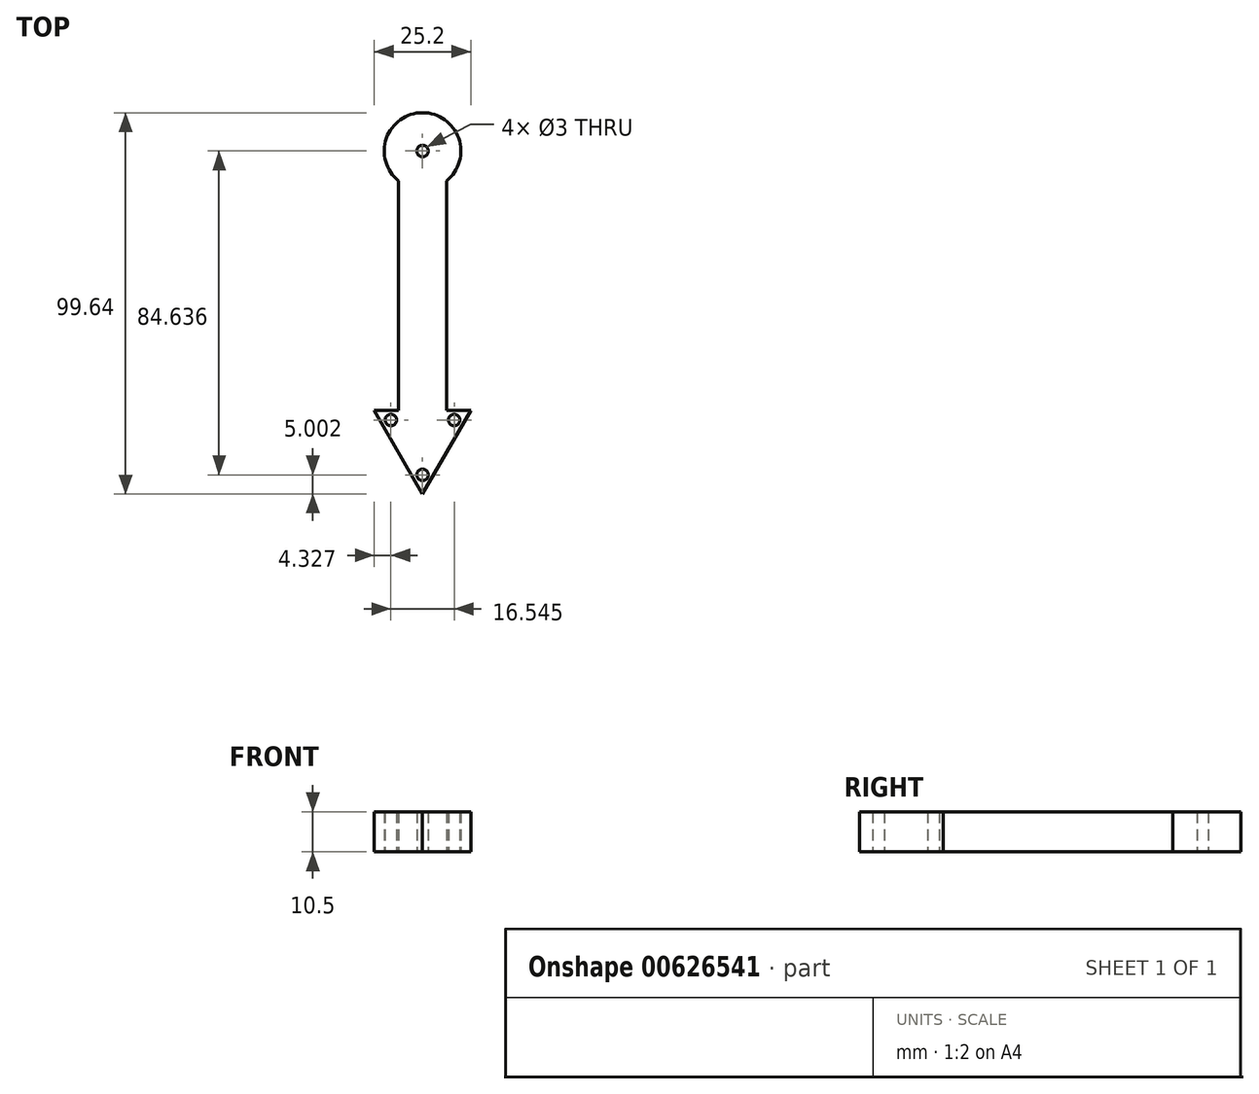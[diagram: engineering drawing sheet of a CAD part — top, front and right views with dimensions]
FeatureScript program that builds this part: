
annotation { "Feature Type Name" : "Feature", "Feature Type Description" : "" }
export const myFeature = defineFeature(function(context is Context, id is Id, definition is map)
    precondition{}
    {
        {
            var Q0;
            Q0=qCreatedBy(makeId("Top.planeOp"),FACE);
            var sketch = newSketch(context, id + "F0", { "sketchPlane" : qUnion([Q0])});
            skCircle(sketch, "E0", {"center": v(0, 38.1) * mm, "radius": 10 * mm});
            skLineSegment(sketch, "E1", {"start": v(-6.25, 30.3) * mm, "end": v(-6.25, -29.7) * mm});
            skCircle(sketch, "E2", {"center": v(0, 38.1) * mm, "radius": 1.5 * mm});
            skLineSegment(sketch, "E3", {"start": v(-12.6, -29.7) * mm, "end": v(0, -51.54) * mm});
            skLineSegment(sketch, "E4", {"start": v(12.6, -29.7) * mm, "end": v(0, -51.54) * mm});
            skLineSegment(sketch, "E5", {"start": v(12.6, -29.7) * mm, "end": v(-12.6, -29.7) * mm});
            skLineSegment(sketch, "E6.MirrorCS", {"start": v(6.25, 30.3) * mm, "end": v(6.25, -29.7) * mm});
            skLineSegment(sketch, "E7", {"start": v(-6.25, -29.7) * mm, "end": v(6.25, -29.7) * mm});
            skPoint(sketch, "E8", {"position": v(0, -29.7) * mm});
            skLineSegment(sketch, "E9", {"start": v(0, -51.54) * mm, "end": v(0, -46.54) * mm, "construction": true});
            skLineSegment(sketch, "E10", {"start": v(12.6, -29.7) * mm, "end": v(8.27, -32.2) * mm, "construction": true});
            skLineSegment(sketch, "E11", {"start": v(-12.6, -29.7) * mm, "end": v(-8.27, -32.2) * mm, "construction": true});
            skCircle(sketch, "E12", {"center": v(0, -46.54) * mm, "radius": 1.5 * mm});
            skCircle(sketch, "E13", {"center": v(-8.27, -32.2) * mm, "radius": 1.5 * mm});
            skCircle(sketch, "E14", {"center": v(8.27, -32.2) * mm, "radius": 1.5 * mm});
            skSolve(sketch);
        }
        {
            var Q0;
            Q0=makeQuery(id+"F0.imprint","IMPRINT",FACE,{"disambiguationData":[TD([[makeQuery(id+"F0.imprint","IMPRINT",EDGE,{"derivedFrom":sQuery(id+"F0.wireOp",EDGE,"E2")}),-1.0]])]});
            var Q1;
            {var subQ7=sQuery(id+"F0.wireOp",EDGE,"E1");Q1=makeQuery(id+"F0.imprint","IMPRINT",FACE,{"disambiguationData":[TD([[makeQuery(id+"F0.imprint","IMPRINT",EDGE,{"derivedFrom":subQ7}),1.0]])]});}
            var Q2;
            {var subQ1=sQuery(id+"F0.wireOp",EDGE,"E3");Q2=makeQuery(id+"F0.imprint","IMPRINT",FACE,{"disambiguationData":[TD([[makeQuery(id+"F0.imprint","IMPRINT",EDGE,{"derivedFrom":subQ1}),1.0]])]});}
            extrude(context, id + "F1", {"entities" : qUnion([Q0, Q1, Q2]), "depth" : 10.5 * mm, "offsetDistance" : 25 * mm});
        }
    });
